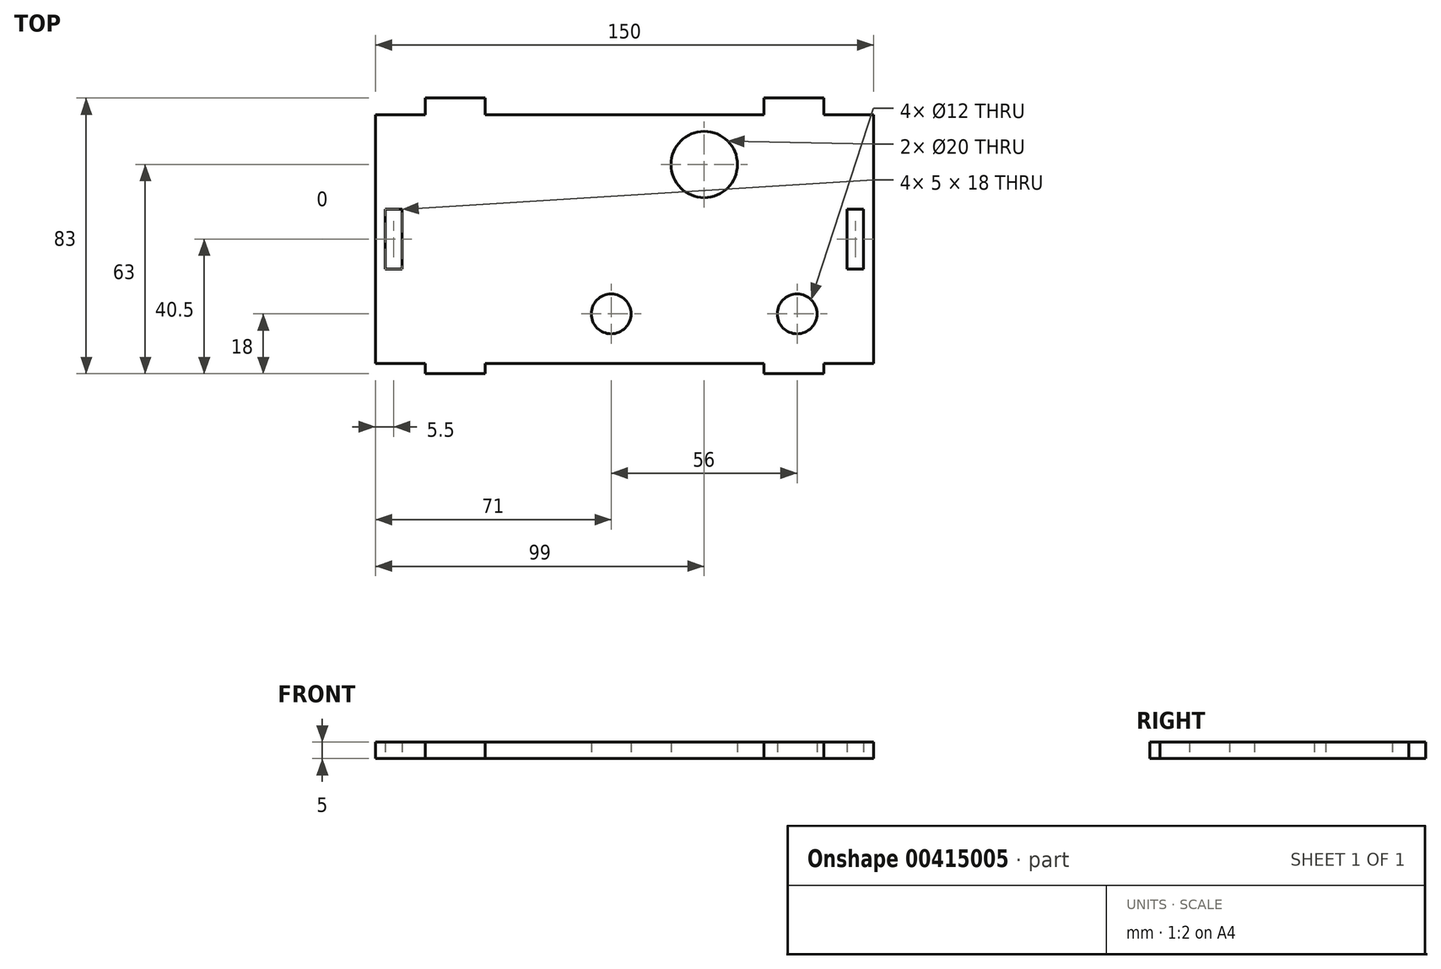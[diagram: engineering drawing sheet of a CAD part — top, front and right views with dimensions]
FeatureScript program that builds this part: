
annotation { "Feature Type Name" : "Feature", "Feature Type Description" : "" }
export const myFeature = defineFeature(function(context is Context, id is Id, definition is map)
    precondition{}
    {
        {
            var Q0;
            Q0=qCreatedBy(makeId("Top.planeOp"),FACE);
            var sketch = newSketch(context, id + "F0", { "sketchPlane" : qUnion([Q0])});
            skLineSegment(sketch, "E0.bottom", {"start": v(75, 37.5) * mm, "end": v(60, 37.5) * mm});
            skLineSegment(sketch, "E0.top", {"start": v(75, -37.5) * mm, "end": v(60, -37.5) * mm});
            skPoint(sketch, "E0.middle", {"position": v(0, 0) * mm});
            skLineSegment(sketch, "E1.top", {"start": v(42, -40.5) * mm, "end": v(60, -40.5) * mm});
            skLineSegment(sketch, "E1.left", {"start": v(42, -37.5) * mm, "end": v(42, -40.5) * mm});
            skLineSegment(sketch, "E1.right", {"start": v(60, -37.5) * mm, "end": v(60, -40.5) * mm});
            skLineSegment(sketch, "E2.top", {"start": v(-60, -40.5) * mm, "end": v(-42, -40.5) * mm});
            skLineSegment(sketch, "E2.left", {"start": v(-60, -37.5) * mm, "end": v(-60, -40.5) * mm});
            skLineSegment(sketch, "E2.right", {"start": v(-42, -37.5) * mm, "end": v(-42, -40.5) * mm});
            skLineSegment(sketch, "E3.trimOffspring", {"start": v(-60, 37.5) * mm, "end": v(-75, 37.5) * mm});
            skLineSegment(sketch, "E4.trimOffspring", {"start": v(42, 37.5) * mm, "end": v(-42, 37.5) * mm});
            skLineSegment(sketch, "E5.trimOffspring", {"start": v(42, -37.5) * mm, "end": v(-42, -37.5) * mm});
            skLineSegment(sketch, "E6.trimOffspring", {"start": v(-60, -37.5) * mm, "end": v(-75, -37.5) * mm});
            skLineSegment(sketch, "E7", {"start": v(0, 0) * mm, "end": v(0, 8.47) * mm, "construction": true});
            skLineSegment(sketch, "E8", {"start": v(0, 0) * mm, "end": v(7.23, 0) * mm, "construction": true});
            skLineSegment(sketch, "E9", {"start": v(-75, 37.5) * mm, "end": v(-75, -37.5) * mm});
            skLineSegment(sketch, "E10", {"start": v(75, 37.5) * mm, "end": v(75, -37.5) * mm});
            skLineSegment(sketch, "E11.bottom", {"start": v(-72, 9) * mm, "end": v(-67, 9) * mm});
            skLineSegment(sketch, "E11.top", {"start": v(-72, -9) * mm, "end": v(-67, -9) * mm});
            skLineSegment(sketch, "E11.left", {"start": v(-72, 9) * mm, "end": v(-72, -9) * mm});
            skLineSegment(sketch, "E11.right", {"start": v(-67, 9) * mm, "end": v(-67, -9) * mm});
            skLineSegment(sketch, "E12.bottom", {"start": v(67, 9) * mm, "end": v(72, 9) * mm});
            skLineSegment(sketch, "E12.top", {"start": v(67, -9) * mm, "end": v(72, -9) * mm});
            skLineSegment(sketch, "E12.left", {"start": v(67, 9) * mm, "end": v(67, -9) * mm});
            skLineSegment(sketch, "E12.right", {"start": v(72, 9) * mm, "end": v(72, -9) * mm});
            skCircle(sketch, "E13", {"center": v(52, -22.5) * mm, "radius": 6 * mm});
            skCircle(sketch, "E14", {"center": v(-4, -22.5) * mm, "radius": 6 * mm});
            skCircle(sketch, "E15", {"center": v(24, 22.5) * mm, "radius": 10 * mm});
            skLineSegment(sketch, "E16", {"start": v(-60, 37.5) * mm, "end": v(-60, 42.5) * mm});
            skLineSegment(sketch, "E17", {"start": v(-60, 42.5) * mm, "end": v(-42, 42.5) * mm});
            skLineSegment(sketch, "E18", {"start": v(-42, 42.5) * mm, "end": v(-42, 37.5) * mm});
            skLineSegment(sketch, "E19.MirrorCS", {"start": v(42, 42.5) * mm, "end": v(42, 37.5) * mm});
            skLineSegment(sketch, "E20.MirrorCS", {"start": v(60, 42.5) * mm, "end": v(42, 42.5) * mm});
            skLineSegment(sketch, "E21.MirrorCS", {"start": v(60, 37.5) * mm, "end": v(60, 42.5) * mm});
            skLineSegment(sketch, "E22", {"start": v(-4, -22.5) * mm, "end": v(52, -22.5) * mm, "construction": true});
            skLineSegment(sketch, "E23", {"start": v(24, -22.5) * mm, "end": v(24, -18.71) * mm, "construction": true});
            skSolve(sketch);
        }
        {
            var Q0;
            Q0=makeQuery(id+"F0.imprint","IMPRINT",FACE,{"disambiguationData":[TD([[makeQuery(id+"F0.imprint","IMPRINT",EDGE,{"derivedFrom":sQuery(id+"F0.wireOp",EDGE,"E0.bottom")}),1.0]])]});
            extrude(context, id + "F1", {"entities" : qUnion([Q0]), "depth" : 5 * mm});
        }
    });
